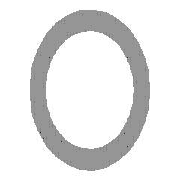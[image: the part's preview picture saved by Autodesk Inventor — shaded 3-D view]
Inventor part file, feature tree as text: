
AUTODESK INVENTOR PART (.ipt)
format: ipt  version: 2021 (Build 250183000, 183)  size: 319,488 bytes
history: native  units: mm (DEFAULTED — no unit token found)
features: other x13, plane x4, sketch x3, sweep x1, split x1
ambient origin geometry x8: Origin, YZ Plane, XZ Plane, XY Plane, X Axis, Y Axis, Z Axis, Center Point
bodies: Solid1 (feature_tree)
feature tree (22):
  parser-record x1  (decoder bookkeeping rows leaked as tree rows — omitted from the tree; the rows remain in map.json)
  other  "Driven Length"
  other  "Plano inicial"
  other  "Plano final"
  other  "Trayectoria de barrido"
  plane  "Plano de trabajo de orientación"
  sweep  "Cuerpo"
  plane  "Plano de trabajo8"
  split  "Dividir4"
  plane  "Plano de trabajo9"
  sketch  "Sketch3"  dims[d0=26.67mm d1=2.8702mm]
  plane  "Work Plane3"
  sketch  "Sketch4"  dims[d4=-0.0mm]
  sketch  "Boceto8"  dims[d5=505.770567mm d6=90.0deg d7=505.770567mm d8=0.0mm d9=0.0mm d26=10.0mm d31=10.0mm d216=0.0mm d217=90.0deg d218=0.0mm d219=90.0deg d220=5.0mm d221=0.0mm d222=5.0mm d223=0.0mm d224=7.0mm]
  other  "Sup148"
  other  "Sup150"
  other  "Sup151"
  other  "Sólido50"
  other  "SuperficieSolevación4"
  other  "Sup149"
  other  "Superficie de contorno97"
  other  "Superficie de contorno98"
